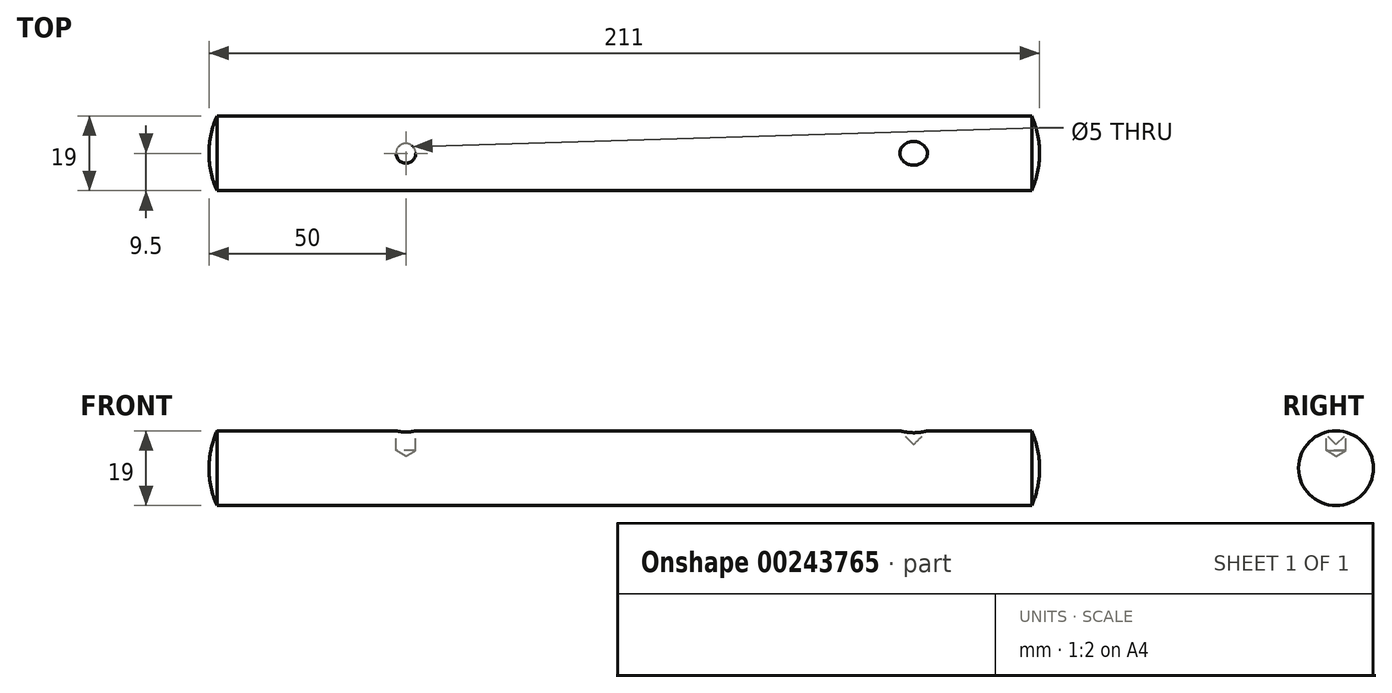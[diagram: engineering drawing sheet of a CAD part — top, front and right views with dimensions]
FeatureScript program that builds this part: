
annotation { "Feature Type Name" : "Feature", "Feature Type Description" : "" }
export const myFeature = defineFeature(function(context is Context, id is Id, definition is map)
    precondition{}
    {
        {
            var Q0;
            Q0=qCreatedBy(makeId("Front.planeOp"),FACE);
            var sketch = newSketch(context, id + "F0", { "sketchPlane" : qUnion([Q0])});
            skLineSegment(sketch, "E0", {"start": v(2, 9.5) * mm, "end": v(209, 9.5) * mm});
            skLineSegment(sketch, "E1", {"start": v(211, 30.42) * mm, "end": v(211, -11.42) * mm, "construction": true});
            skLineSegment(sketch, "E2", {"start": v(-17.94, 0) * mm, "end": v(226.7, 0) * mm, "construction": true});
            skLineSegment(sketch, "E3", {"start": v(2, 12.52) * mm, "end": v(2, -13.41) * mm, "construction": true});
            skLineSegment(sketch, "E4.MirrorCS", {"start": v(-8.24, -9.5) * mm, "end": v(219.38, -9.5) * mm, "construction": true});
            skArc(sketch, "E5", {"start": v(2, 9.5) * mm, "mid": v(0.5, 4.85) * mm, "end": v(0, 0) * mm});
            skArc(sketch, "E6", {"start": v(0, 0) * mm, "mid": v(0.5, -4.85) * mm, "end": v(2, -9.5) * mm, "construction": true});
            skPoint(sketch, "E7", {"position": v(211, 0) * mm});
            skLineSegment(sketch, "E8", {"start": v(209, 12.7) * mm, "end": v(209, -11.42) * mm, "construction": true});
            skArc(sketch, "E9", {"start": v(209, -9.5) * mm, "mid": v(210.5, -4.85) * mm, "end": v(211, 0) * mm, "construction": true});
            skArc(sketch, "E10", {"start": v(211, 0) * mm, "mid": v(210.5, 4.85) * mm, "end": v(209, 9.5) * mm});
            skPoint(sketch, "E11.orphan", {"position": v(-8.24, 9.5) * mm});
            skLineSegment(sketch, "E12", {"start": v(0, 0) * mm, "end": v(211, 0) * mm});
            skSolve(sketch);
        }
        {
            var Q0;
            Q0=makeQuery(id+"F0.imprint","IMPRINT",FACE,{"disambiguationData":[TD([[makeQuery(id+"F0.imprint","IMPRINT",EDGE,{"derivedFrom":sQuery(id+"F0.wireOp",EDGE,"E0")}),-1.0]])]});
            var Q1;
            Q1=sQuery(id+"F0.wireOp",EDGE,"E2");
            revolve(context, id + "F1", {"entities" : qUnion([Q0]), "axis" : qUnion([Q1]), "revolveType" : RevolveType.FULL});
        }
        {
            var Q0;
            Q0=qCreatedBy(makeId("Top.planeOp"),FACE);
            cPlane(context, id + "F2", {"entities" : qUnion([Q0]), "cplaneType" : CPlaneType.OFFSET, "offset" : 9.5 * mm, "width" : 150 * mm, "height" : 150 * mm});
        }
        {
            var Q0;
            Q0=qCreatedBy(id+"F2.planeOp",FACE);
            var sketch = newSketch(context, id + "F3", { "sketchPlane" : qUnion([Q0])});
            skPoint(sketch, "E13", {"position": v(50, 0) * mm});
            skLineSegment(sketch, "E14", {"start": v(211, 42.48) * mm, "end": v(211, -28.24) * mm, "construction": true});
            skSolve(sketch);
        }
        {
            var Q0;
            Q0=sQuery(id+"F3.wireOp",VERTEX,"E13");
            var Q1;
            Q1=makeQuery(id+"F1.opRevolve","SWEPT_BODY",BODY,{"disambiguationData":[OSD([sQuery(id+"F0.wireOp",EDGE,"E0"),sQuery(id+"F0.wireOp",EDGE,"E5"),sQuery(id+"F0.wireOp",EDGE,"E10"),sQuery(id+"F0.wireOp",EDGE,"E12")])]});
            hole(context, id + "F4", {"style" : HoleStyle.SIMPLE, "endStyle" : HoleEndStyle.BLIND, "holeDiameter" : 5 * mm, "holeDepth" : 5 * mm, "startFromSketch" : true, "locations" : qUnion([Q0]), "scope" : qUnion([Q1])});
        }
        {
            var Q0;
            Q0=qCreatedBy(makeId("Front.planeOp"),FACE);
            var sketch = newSketch(context, id + "F5", { "sketchPlane" : qUnion([Q0])});
            skLineSegment(sketch, "E15", {"start": v(179, 16.62) * mm, "end": v(179, -16.68) * mm, "construction": true});
            skLineSegment(sketch, "E16", {"start": v(179, 11.5) * mm, "end": v(184.5, 11.5) * mm});
            skLineSegment(sketch, "E17", {"start": v(184.5, 11.5) * mm, "end": v(179, 6) * mm});
            skLineSegment(sketch, "E18", {"start": v(179, 6) * mm, "end": v(179, 11.5) * mm});
            skPoint(sketch, "E19", {"position": v(182.5, 9.5) * mm});
            skSolve(sketch);
        }
        {
            var Q0;
            Q0=makeQuery(id+"F5.imprint","IMPRINT",FACE,{"disambiguationData":[TD([[makeQuery(id+"F5.imprint","IMPRINT",EDGE,{"derivedFrom":sQuery(id+"F5.wireOp",EDGE,"E16")}),-1.0]])]});
            var Q1;
            Q1=sQuery(id+"F5.wireOp",EDGE,"E15");
            revolve(context, id + "F6", {"operationType" : NewBodyOperationType.REMOVE, "entities" : qUnion([Q0]), "axis" : qUnion([Q1]), "revolveType" : RevolveType.FULL, "oppositeDirection" : true});
        }
    });
